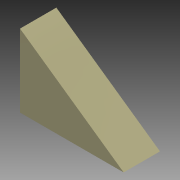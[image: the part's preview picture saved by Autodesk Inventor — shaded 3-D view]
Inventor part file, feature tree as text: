
AUTODESK INVENTOR PART (.ipt)
format: ipt  version: 2013 (Build 170138000, 138)  size: 68,608 bytes
history: native  units: in
note: dims shown in document units (in); Inventor stores cm internally (conversion verified against a paired STEP export)
features: extrude x1, sketch x1
ambient origin geometry x8: Origin, YZ Plane, XZ Plane, XY Plane, X Axis, Y Axis, Z Axis, Center Point
bodies: Solid1 (feature_tree)
feature tree (2):
  extrude  "Extrusion1"  Depth=2.0in
  sketch  "Sketch1"  dims[d0=2.85in d1=2.0in d2=90.0deg d3=1.0in d4=0.0in]
